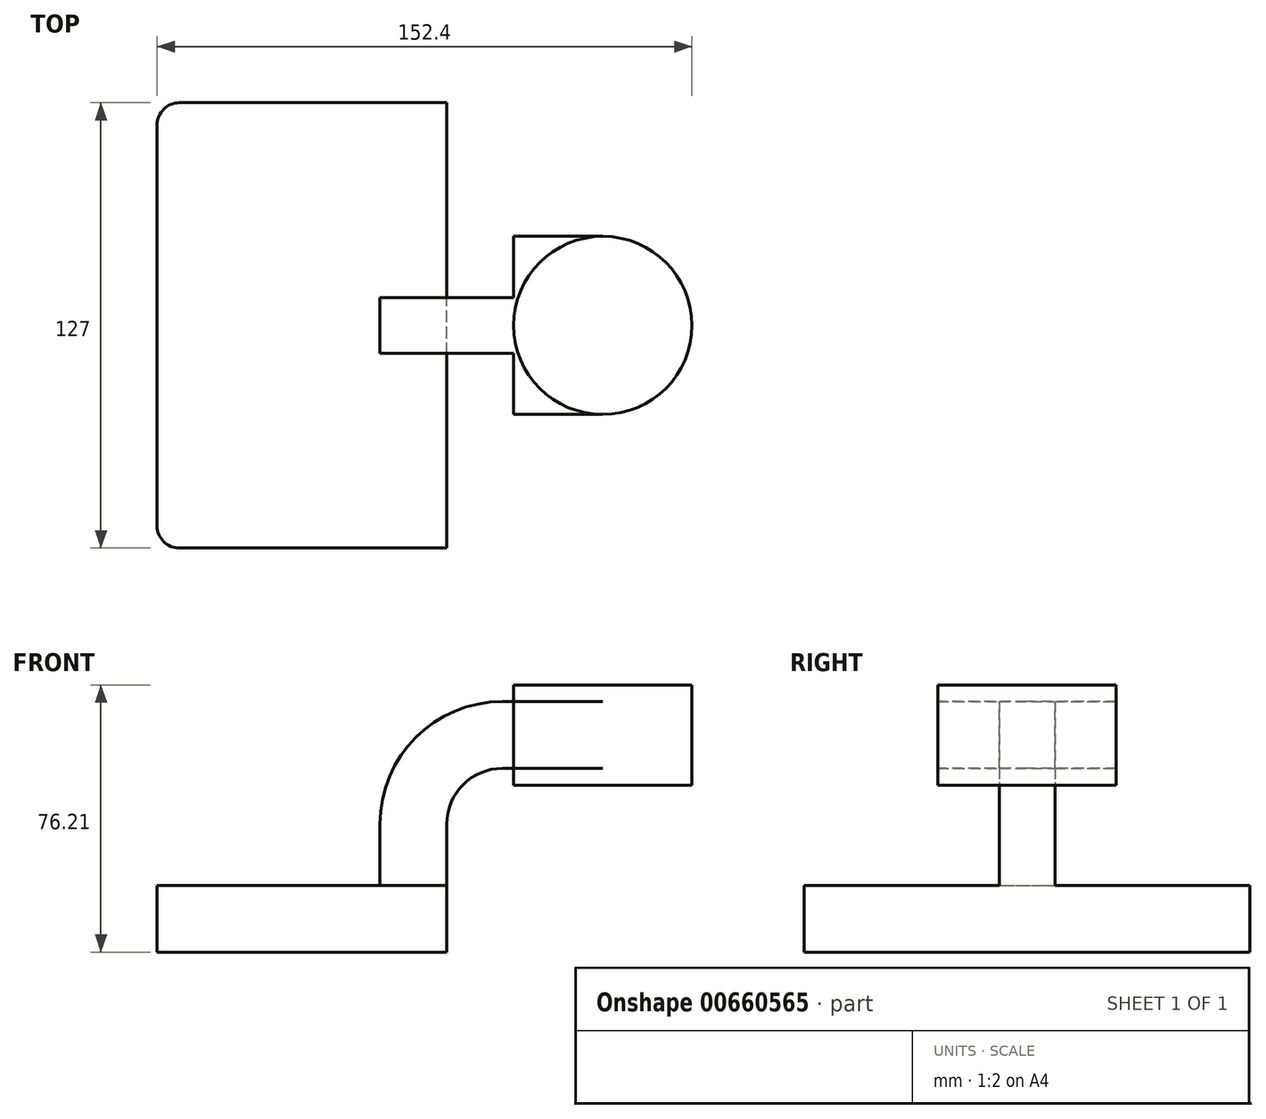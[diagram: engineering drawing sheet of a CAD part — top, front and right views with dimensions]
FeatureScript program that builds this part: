
annotation { "Feature Type Name" : "Feature", "Feature Type Description" : "" }
export const myFeature = defineFeature(function(context is Context, id is Id, definition is map)
    precondition{}
    {
        {
            var Q0;
            Q0=qCreatedBy(makeId("Front.planeOp"),FACE);
            var sketch = newSketch(context, id + "F0", { "sketchPlane" : qUnion([Q0])});
            skLineSegment(sketch, "E0.bottom", {"start": v(-41.28, 9.52) * mm, "end": v(41.28, 9.52) * mm});
            skLineSegment(sketch, "E0.top", {"start": v(-41.27, -9.53) * mm, "end": v(41.27, -9.53) * mm});
            skLineSegment(sketch, "E0.left", {"start": v(-41.27, -9.53) * mm, "end": v(-41.28, 9.52) * mm});
            skLineSegment(sketch, "E0.right", {"start": v(41.28, -9.53) * mm, "end": v(41.28, 9.52) * mm});
            skPoint(sketch, "E0.middle", {"position": v(0, 0) * mm});
            skLineSegment(sketch, "E1.bottom", {"start": v(111.12, 38.1) * mm, "end": v(60.32, 38.1) * mm});
            skLineSegment(sketch, "E1.top", {"start": v(111.12, 66.67) * mm, "end": v(60.32, 66.67) * mm});
            skLineSegment(sketch, "E1.left", {"start": v(111.12, 38.1) * mm, "end": v(111.12, 66.67) * mm});
            skLineSegment(sketch, "E1.right", {"start": v(60.32, 38.1) * mm, "end": v(60.32, 66.67) * mm});
            skPoint(sketch, "E1.middle", {"position": v(85.72, 52.39) * mm});
            skLineSegment(sketch, "E2", {"start": v(41.27, -9.53) * mm, "end": v(41.27, 27) * mm});
            skArc(sketch, "E3", {"start": v(41.27, 27) * mm, "mid": v(45.92, 38.23) * mm, "end": v(57.15, 42.88) * mm});
            skLineSegment(sketch, "E4", {"start": v(57.15, 42.88) * mm, "end": v(85.72, 42.88) * mm});
            skLineSegment(sketch, "E5", {"start": v(41.28, 9.52) * mm, "end": v(41.28, 27) * mm});
            skLineSegment(sketch, "E6.0", {"start": v(57.15, 61.93) * mm, "end": v(85.72, 61.93) * mm});
            skArc(sketch, "E6.1", {"start": v(22.23, 27) * mm, "mid": v(32.45, 51.7) * mm, "end": v(57.15, 61.93) * mm});
            skLineSegment(sketch, "E6.2", {"start": v(22.22, 9.52) * mm, "end": v(22.22, 27) * mm});
            skLineSegment(sketch, "E7", {"start": v(85.72, 38.1) * mm, "end": v(85.72, 66.67) * mm});
            skFitSpline(sketch, "E8", {"points": [v(-41.28, 9.52) * mm, v(57.15, 61.93) * mm], "startDerivative": vector(4.83, 101.24) * mm, "endDerivative": vector(120.76, -5.86) * mm});
            skSolve(sketch);
        }
        {
            var Q0;
            Q0=makeQuery(id+"F0.imprint","IMPRINT",FACE,{"disambiguationData":[TD([[makeQuery(id+"F0.imprint","IMPRINT",EDGE,{"derivedFrom":sQuery(id+"F0.wireOp",EDGE,"E0.top")}),1.0]])]});
            extrude(context, id + "F1", {"entities" : qUnion([Q0]), "endBound" : BoundingType.SYMMETRIC, "depth" : 127 * mm, "offsetDistance" : 25.4 * mm});
        }
        {
            var Q0;
            {var subQ1=sQuery(id+"F0.wireOp",EDGE,"E3");Q0=makeQuery(id+"F0.imprint","IMPRINT",FACE,{"disambiguationData":[TD([[makeQuery(id+"F0.imprint","IMPRINT",EDGE,{"derivedFrom":subQ1}),1.0]])]});}
            var Q1;
            {var subQ0=sQuery(id+"F0.wireOp",EDGE,"E4");var subQ1=sQuery(id+"F0.wireOp",EDGE,"E1.right");var subQ2=makeQuery(id+"F0.imprint","INTERSECT",VERTEX,{"derivedFrom":[subQ1,subQ0]});Q1=makeQuery(id+"F0.imprint","IMPRINT",FACE,{"disambiguationData":[TD([[makeQuery(id+"F0.imprint","IMPRINT",EDGE,{"disambiguationData":[TD([[subQ2,-1.0]])],"derivedFrom":subQ1}),-1.0]])]});}
            extrude(context, id + "F2", {"entities" : qUnion([Q0, Q1]), "operationType" : NewBodyOperationType.ADD, "endBound" : BoundingType.SYMMETRIC, "depth" : 50.8 * mm, "offsetDistance" : 25.4 * mm});
        }
        {
            var Q0;
            Q0=makeQuery(id+"F0.imprint","IMPRINT",FACE,{"disambiguationData":[TD([[makeQuery(id+"F0.imprint","IMPRINT",EDGE,{"derivedFrom":sQuery(id+"F0.wireOp",EDGE,"E6.1")}),1.0]])]});
            extrude(context, id + "F3", {"entities" : qUnion([Q0]), "operationType" : NewBodyOperationType.ADD, "endBound" : BoundingType.SYMMETRIC, "depth" : 15.88 * mm, "offsetDistance" : 25.4 * mm});
        }
        {
            var Q0;
            {var subQ0=sQuery(id+"F0.wireOp",EDGE,"E1.left");Q0=makeQuery(id+"F0.imprint","IMPRINT",FACE,{"disambiguationData":[TD([[makeQuery(id+"F0.imprint","IMPRINT",EDGE,{"derivedFrom":subQ0}),1.0]])]});}
            var Q1;
            Q1=sQuery(id+"F0.wireOp",EDGE,"E7");
            revolve(context, id + "F4", {"operationType" : NewBodyOperationType.ADD, "entities" : qUnion([Q0]), "axis" : qUnion([Q1]), "revolveType" : RevolveType.FULL});
        }
        {
            var Q0;
            Q0=makeQuery(id+"F1.opExtrude","CAP_EDGE",EDGE,{"disambiguationData":[OSD([sQuery(id+"F0.wireOp",EDGE,"E2")])],"isStart":false});
            var Q1;
            Q1=makeQuery(id+"F1.opExtrude","CAP_EDGE",EDGE,{"disambiguationData":[OSD([sQuery(id+"F0.wireOp",EDGE,"E0.left")])],"isStart":false});
            var Q2;
            Q2=makeQuery(id+"F1.opExtrude","CAP_EDGE",EDGE,{"disambiguationData":[OSD([sQuery(id+"F0.wireOp",EDGE,"E0.left")])],"isStart":true});
            var Q3;
            Q3=makeQuery(id+"F1.opExtrude","CAP_EDGE",EDGE,{"disambiguationData":[OSD([sQuery(id+"F0.wireOp",EDGE,"E2")])],"isStart":true});
            fillet(context, id + "F5", {"entities" : qUnion([Q0, Q1, Q2, Q3]), "radius" : 6.35 * mm, "tangentPropagation" : true, "allowEdgeOverflow" : false});
        }
    });
